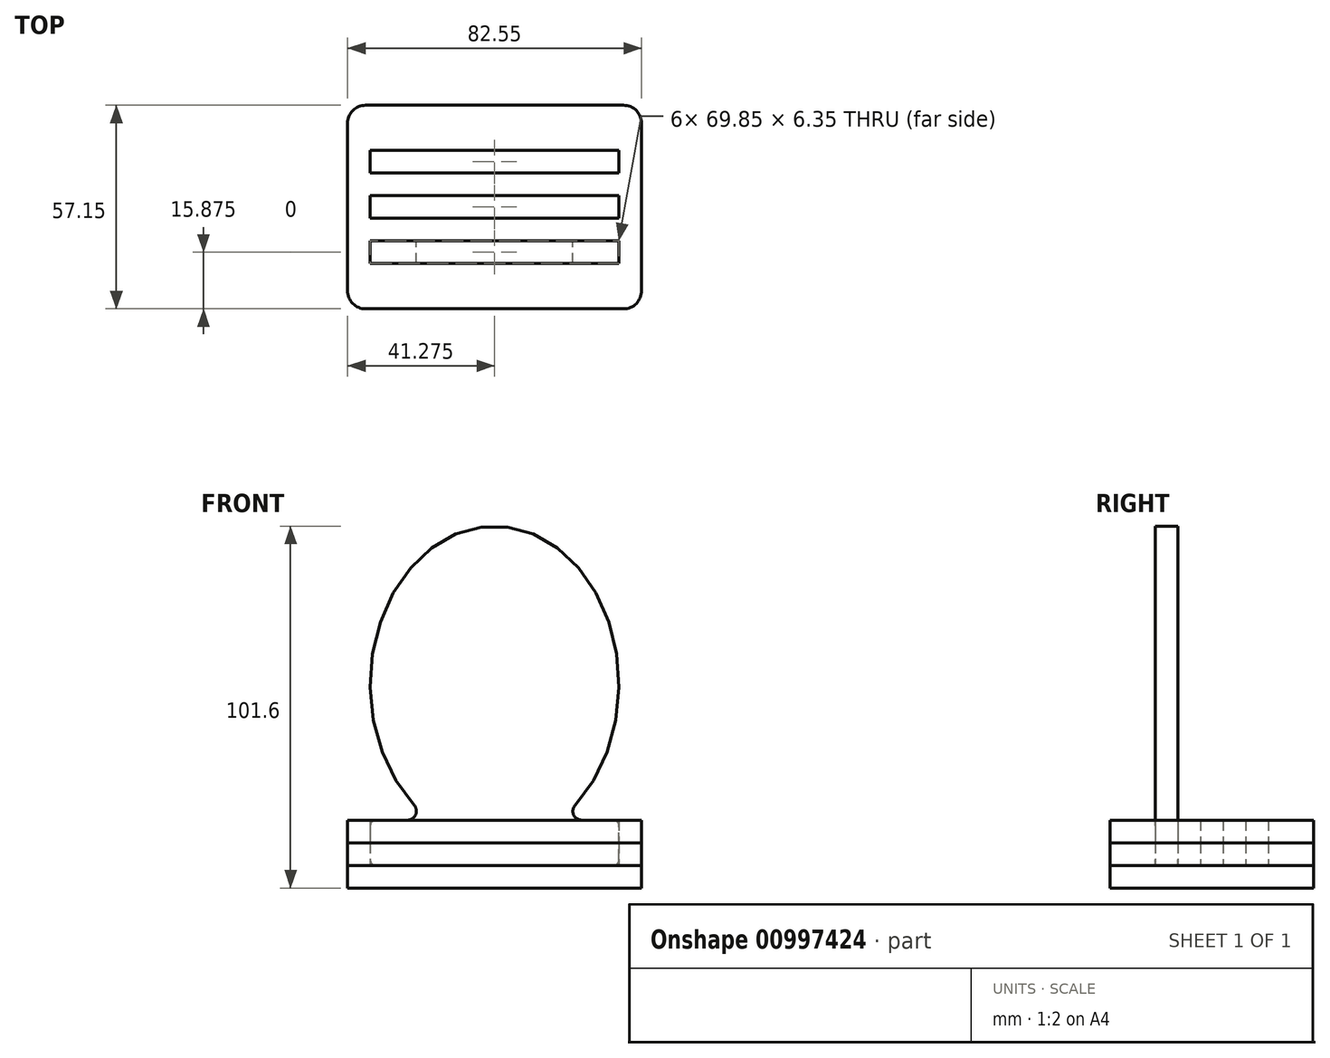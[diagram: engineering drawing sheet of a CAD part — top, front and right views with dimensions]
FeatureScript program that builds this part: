
annotation { "Feature Type Name" : "Feature", "Feature Type Description" : "" }
export const myFeature = defineFeature(function(context is Context, id is Id, definition is map)
    precondition{}
    {
        {
            var Q0;
            Q0=qCreatedBy(makeId("Top.planeOp"),FACE);
            var sketch = newSketch(context, id + "F0", { "sketchPlane" : qUnion([Q0])});
            skLineSegment(sketch, "E0.bottom", {"start": v(0, 0) * mm, "end": v(82.55, 0) * mm});
            skLineSegment(sketch, "E0.top", {"start": v(0, 57.15) * mm, "end": v(82.55, 57.15) * mm});
            skLineSegment(sketch, "E0.left", {"start": v(0, 0) * mm, "end": v(0, 57.15) * mm});
            skLineSegment(sketch, "E0.right", {"start": v(82.55, 0) * mm, "end": v(82.55, 57.15) * mm});
            skLineSegment(sketch, "E1.bottom", {"start": v(6.35, 19.05) * mm, "end": v(76.2, 19.05) * mm});
            skLineSegment(sketch, "E1.top", {"start": v(6.35, 12.7) * mm, "end": v(76.2, 12.7) * mm});
            skLineSegment(sketch, "E1.left", {"start": v(6.35, 19.05) * mm, "end": v(6.35, 12.7) * mm});
            skLineSegment(sketch, "E1.right", {"start": v(76.2, 19.05) * mm, "end": v(76.2, 12.7) * mm});
            skLineSegment(sketch, "E2.0.1.0", {"start": v(6.35, 25.4) * mm, "end": v(76.2, 25.4) * mm});
            skLineSegment(sketch, "E2.0.1.1", {"start": v(6.35, 31.75) * mm, "end": v(6.35, 25.4) * mm});
            skLineSegment(sketch, "E2.0.1.2", {"start": v(76.2, 31.75) * mm, "end": v(76.2, 25.4) * mm});
            skLineSegment(sketch, "E2.0.1.3", {"start": v(6.35, 31.75) * mm, "end": v(76.2, 31.75) * mm});
            skLineSegment(sketch, "E2.0.2.0", {"start": v(6.35, 38.1) * mm, "end": v(76.2, 38.1) * mm});
            skLineSegment(sketch, "E2.0.2.1", {"start": v(6.35, 44.45) * mm, "end": v(6.35, 38.1) * mm});
            skLineSegment(sketch, "E2.0.2.2", {"start": v(76.2, 44.45) * mm, "end": v(76.2, 38.1) * mm});
            skLineSegment(sketch, "E2.0.2.3", {"start": v(6.35, 44.45) * mm, "end": v(76.2, 44.45) * mm});
            skLineSegment(sketch, "E2.direction1", {"start": v(6.35, 12.7) * mm, "end": v(6.35, 12.7) * mm});
            skLineSegment(sketch, "E2.direction2", {"start": v(6.35, 12.7) * mm, "end": v(6.35, 25.4) * mm, "construction": true});
            skSolve(sketch);
        }
        {
            var Q0;
            Q0=makeQuery(id+"F0.imprint","IMPRINT",FACE,{"disambiguationData":[TD([[makeQuery(id+"F0.imprint","IMPRINT",EDGE,{"derivedFrom":sQuery(id+"F0.wireOp",EDGE,"E0.bottom")}),1.0]])]});
            var Q1;
            Q1=makeQuery(id+"F0.imprint","IMPRINT",FACE,{"disambiguationData":[TD([[makeQuery(id+"F0.imprint","IMPRINT",EDGE,{"derivedFrom":sQuery(id+"F0.wireOp",EDGE,"E1.bottom")}),-1.0]])]});
            var Q2;
            Q2=makeQuery(id+"F0.imprint","IMPRINT",FACE,{"disambiguationData":[TD([[makeQuery(id+"F0.imprint","IMPRINT",EDGE,{"derivedFrom":sQuery(id+"F0.wireOp",EDGE,"E2.0.1.0")}),1.0]])]});
            var Q3;
            Q3=makeQuery(id+"F0.imprint","IMPRINT",FACE,{"disambiguationData":[TD([[makeQuery(id+"F0.imprint","IMPRINT",EDGE,{"derivedFrom":sQuery(id+"F0.wireOp",EDGE,"E2.0.2.0")}),1.0]])]});
            extrude(context, id + "F1", {"entities" : qUnion([Q0, Q1, Q2, Q3]), "oppositeDirection" : true, "depth" : 6.35 * mm, "offsetDistance" : 25.4 * mm});
        }
        {
            var Q0;
            Q0=makeQuery(id+"F0.imprint","IMPRINT",FACE,{"disambiguationData":[TD([[makeQuery(id+"F0.imprint","IMPRINT",EDGE,{"derivedFrom":sQuery(id+"F0.wireOp",EDGE,"E0.bottom")}),1.0]])]});
            extrude(context, id + "F2", {"entities" : qUnion([Q0]), "depth" : 6.35 * mm, "offsetDistance" : 25.4 * mm});
        }
        {
            var Q0;
            Q0=makeQuery(id+"F2.opExtrude","CAP_FACE",FACE,{"disambiguationData":[OSD([sQuery(id+"F0.wireOp",EDGE,"E0.bottom"),sQuery(id+"F0.wireOp",EDGE,"E0.top"),sQuery(id+"F0.wireOp",EDGE,"E0.left"),sQuery(id+"F0.wireOp",EDGE,"E0.right"),sQuery(id+"F0.wireOp",EDGE,"E1.bottom"),sQuery(id+"F0.wireOp",EDGE,"E1.top"),sQuery(id+"F0.wireOp",EDGE,"E1.left"),sQuery(id+"F0.wireOp",EDGE,"E1.right"),sQuery(id+"F0.wireOp",EDGE,"E2.0.1.0"),sQuery(id+"F0.wireOp",EDGE,"E2.0.1.1"),sQuery(id+"F0.wireOp",EDGE,"E2.0.1.2"),sQuery(id+"F0.wireOp",EDGE,"E2.0.1.3"),sQuery(id+"F0.wireOp",EDGE,"E2.0.2.0"),sQuery(id+"F0.wireOp",EDGE,"E2.0.2.1"),sQuery(id+"F0.wireOp",EDGE,"E2.0.2.2"),sQuery(id+"F0.wireOp",EDGE,"E2.0.2.3")])],"isStart":false});
            extrude(context, id + "F3", {"entities" : qUnion([Q0]), "depth" : 6.35 * mm, "offsetDistance" : 25.4 * mm});
        }
        {
            var Q0;
            Q0=makeQuery(id+"F3.opExtrude","SWEPT_EDGE",EDGE,{"disambiguationData":[OSD([sQuery(id+"F0.wireOp",EDGE,"E0.bottom"),sQuery(id+"F0.wireOp",EDGE,"E0.right")])]});
            var Q1;
            Q1=makeQuery(id+"F2.opExtrude","SWEPT_EDGE",EDGE,{"disambiguationData":[OSD([sQuery(id+"F0.wireOp",EDGE,"E0.bottom"),sQuery(id+"F0.wireOp",EDGE,"E0.right")])]});
            var Q2;
            Q2=makeQuery(id+"F1.opExtrude","SWEPT_EDGE",EDGE,{"disambiguationData":[OSD([sQuery(id+"F0.wireOp",EDGE,"E0.bottom"),sQuery(id+"F0.wireOp",EDGE,"E0.right")])]});
            var Q3;
            Q3=makeQuery(id+"F3.opExtrude","SWEPT_EDGE",EDGE,{"disambiguationData":[OSD([sQuery(id+"F0.wireOp",EDGE,"E0.bottom"),sQuery(id+"F0.wireOp",EDGE,"E0.left")])]});
            var Q4;
            Q4=makeQuery(id+"F2.opExtrude","SWEPT_EDGE",EDGE,{"disambiguationData":[OSD([sQuery(id+"F0.wireOp",EDGE,"E0.bottom"),sQuery(id+"F0.wireOp",EDGE,"E0.left")])]});
            var Q5;
            Q5=makeQuery(id+"F1.opExtrude","SWEPT_EDGE",EDGE,{"disambiguationData":[OSD([sQuery(id+"F0.wireOp",EDGE,"E0.bottom"),sQuery(id+"F0.wireOp",EDGE,"E0.left")])]});
            var Q6;
            Q6=makeQuery(id+"F3.opExtrude","SWEPT_EDGE",EDGE,{"disambiguationData":[OSD([sQuery(id+"F0.wireOp",EDGE,"E0.top"),sQuery(id+"F0.wireOp",EDGE,"E0.left")])]});
            var Q7;
            Q7=makeQuery(id+"F2.opExtrude","SWEPT_EDGE",EDGE,{"disambiguationData":[OSD([sQuery(id+"F0.wireOp",EDGE,"E0.top"),sQuery(id+"F0.wireOp",EDGE,"E0.left")])]});
            var Q8;
            Q8=makeQuery(id+"F1.opExtrude","SWEPT_EDGE",EDGE,{"disambiguationData":[OSD([sQuery(id+"F0.wireOp",EDGE,"E0.top"),sQuery(id+"F0.wireOp",EDGE,"E0.left")])]});
            var Q9;
            Q9=makeQuery(id+"F3.opExtrude","SWEPT_EDGE",EDGE,{"disambiguationData":[OSD([sQuery(id+"F0.wireOp",EDGE,"E0.top"),sQuery(id+"F0.wireOp",EDGE,"E0.right")])]});
            var Q10;
            Q10=makeQuery(id+"F2.opExtrude","SWEPT_EDGE",EDGE,{"disambiguationData":[OSD([sQuery(id+"F0.wireOp",EDGE,"E0.top"),sQuery(id+"F0.wireOp",EDGE,"E0.right")])]});
            var Q11;
            Q11=makeQuery(id+"F1.opExtrude","SWEPT_EDGE",EDGE,{"disambiguationData":[OSD([sQuery(id+"F0.wireOp",EDGE,"E0.top"),sQuery(id+"F0.wireOp",EDGE,"E0.right")])]});
            fillet(context, id + "F4", {"entities" : qUnion([Q0, Q1, Q2, Q3, Q4, Q5, Q6, Q7, Q8, Q9, Q10, Q11]), "radius" : 5.08 * mm, "tangentPropagation" : true, "allowEdgeOverflow" : false});
        }
        {
            var Q0;
            Q0=makeQuery(id+"F3.opExtrude","SWEPT_FACE",FACE,{"disambiguationData":[OSD([sQuery(id+"F0.wireOp",EDGE,"E1.bottom")])]});
            var sketch = newSketch(context, id + "F5", { "sketchPlane" : qUnion([Q0])});
            skLineSegment(sketch, "E3.0.0", {"start": v(6.35, 0) * mm, "end": v(76.2, 0) * mm});
            skLineSegment(sketch, "E3.0.1", {"start": v(76.2, 0) * mm, "end": v(76.2, 6.35) * mm});
            skLineSegment(sketch, "E3.0.2", {"start": v(76.2, 6.35) * mm, "end": v(6.35, 6.35) * mm});
            skLineSegment(sketch, "E3.0.3", {"start": v(6.35, 6.35) * mm, "end": v(6.35, 0) * mm});
            skLineSegment(sketch, "E4.bottom", {"start": v(6.35, 12.7) * mm, "end": v(76.2, 12.7) * mm});
            skLineSegment(sketch, "E4.top", {"start": v(6.35, 6.35) * mm, "end": v(76.2, 6.35) * mm});
            skLineSegment(sketch, "E4.left", {"start": v(6.35, 12.7) * mm, "end": v(6.35, 6.35) * mm});
            skLineSegment(sketch, "E4.right", {"start": v(76.2, 12.7) * mm, "end": v(76.2, 6.35) * mm});
            skEllipse(sketch, "E5", {"center": v(41.28, 50.8) * mm, "majorRadius": 44.45 * mm, "minorRadius": 34.93 * mm, "majorAxis": v(0, 1)});
            skLineSegment(sketch, "E6", {"start": v(41.28, 0) * mm, "end": v(41.28, 109.72) * mm, "construction": true});
            skPoint(sketch, "E7", {"position": v(41.28, 54.86) * mm});
            skFitSpline(sketch, "E8.0", {"points": [v(42.6, 88.87) * mm, v(41.27, 88.91) * mm, v(39.94, 88.87) * mm, v(38.18, 88.7) * mm, v(35.99, 88.29) * mm, v(33.4, 87.46) * mm, v(30.86, 86.3) * mm, v(28.38, 84.82) * mm, v(25.99, 83) * mm, v(24.08, 81.2) * mm, v(22.62, 79.6) * mm, v(21.56, 78.32) * mm, v(20.55, 76.96) * mm, v(19.27, 75.07) * mm, v(17.8, 72.55) * mm, v(16.28, 69.3) * mm, v(15, 65.87) * mm, v(14, 62.27) * mm, v(13.25, 58.54) * mm, v(12.88, 55.35) * mm, v(12.73, 52.76) * mm, v(12.69, 50.8) * mm, v(12.73, 48.84) * mm, v(12.88, 46.25) * mm, v(13.25, 43.06) * mm, v(14, 39.33) * mm, v(15, 35.73) * mm, v(16.28, 32.3) * mm, v(17.8, 29.05) * mm, v(19.27, 26.53) * mm, v(20.55, 24.64) * mm, v(21.56, 23.28) * mm, v(22.62, 22) * mm, v(24.08, 20.4) * mm, v(25.99, 18.6) * mm, v(28.38, 16.78) * mm, v(30.86, 15.3) * mm, v(33.4, 14.14) * mm, v(35.99, 13.31) * mm, v(38.18, 12.9) * mm, v(39.94, 12.73) * mm, v(41.28, 12.69) * mm, v(42.6, 12.73) * mm, v(44.37, 12.9) * mm, v(46.56, 13.31) * mm, v(49.15, 14.14) * mm, v(51.69, 15.3) * mm, v(54.17, 16.78) * mm, v(56.56, 18.6) * mm, v(58.47, 20.4) * mm, v(59.93, 22) * mm, v(60.99, 23.28) * mm, v(62, 24.64) * mm, v(63.28, 26.53) * mm, v(64.75, 29.05) * mm, v(66.27, 32.3) * mm, v(67.55, 35.73) * mm, v(68.56, 39.33) * mm, v(69.3, 43.06) * mm, v(69.67, 46.25) * mm, v(69.82, 48.84) * mm, v(69.86, 50.8) * mm, v(69.82, 52.76) * mm, v(69.67, 55.35) * mm, v(69.3, 58.54) * mm, v(68.56, 62.27) * mm, v(67.55, 65.87) * mm, v(66.27, 69.3) * mm, v(64.75, 72.55) * mm, v(63.28, 75.07) * mm, v(62, 76.96) * mm, v(60.99, 78.32) * mm, v(59.93, 79.6) * mm, v(58.47, 81.2) * mm, v(56.56, 83) * mm, v(54.17, 84.82) * mm, v(51.69, 86.3) * mm, v(49.15, 87.46) * mm, v(46.56, 88.29) * mm, v(44.37, 88.7) * mm, v(42.6, 88.87) * mm, v(41.27, 88.91) * mm, v(39.94, 88.87) * mm, v(42.6, 88.87) * mm]});
            skSolve(sketch);
        }
        {
            var Q0;
            Q0 = qSketchRegion(id + "F5", true);
            extrude(context, id + "F6", {"entities" : qUnion([Q0]), "depth" : 6.35 * mm, "offsetDistance" : 25.4 * mm});
        }
        {
            var Q0;
            {var subQ0=sQuery(id+"F5.wireOp",EDGE,"E5");var subQ1=sQuery(id+"F5.wireOp",EDGE,"E4.bottom");Q0=makeQuery(id+"F6.opExtrude","SWEPT_EDGE",EDGE,{"disambiguationData":[OSD([subQ1,subQ0]),TDD([makeQuery(id+"F5.imprint","INTERSECT",VERTEX,{"disambiguationData":[OD(1.0)],"derivedFrom":[subQ1,subQ0]})])]});}
            var Q1;
            {var subQ0=sQuery(id+"F5.wireOp",EDGE,"E5");var subQ1=sQuery(id+"F5.wireOp",EDGE,"E4.bottom");Q1=makeQuery(id+"F6.opExtrude","SWEPT_EDGE",EDGE,{"disambiguationData":[OSD([subQ1,subQ0]),TDD([makeQuery(id+"F5.imprint","INTERSECT",VERTEX,{"disambiguationData":[OD(0.0)],"derivedFrom":[subQ1,subQ0]})])]});}
            fillet(context, id + "F7", {"entities" : qUnion([Q0, Q1]), "radius" : 2.54 * mm, "tangentPropagation" : true, "allowEdgeOverflow" : false});
        }
        {
            var Q0;
            Q0=makeQuery(id+"F6.opExtrude","SWEPT_EDGE",EDGE,{"disambiguationData":[OSD([sQuery(id+"F5.wireOp",EDGE,"E4.bottom"),sQuery(id+"F5.wireOp",EDGE,"E4.right")])]});
            var Q1;
            Q1=makeQuery(id+"F6.opExtrude","SWEPT_EDGE",EDGE,{"disambiguationData":[OSD([sQuery(id+"F5.wireOp",EDGE,"E4.bottom"),sQuery(id+"F5.wireOp",EDGE,"E4.left")])]});
            var Q2;
            Q2=makeQuery(id+"F6.opExtrude","SWEPT_EDGE",EDGE,{"disambiguationData":[OSD([sQuery(id+"F5.wireOp",EDGE,"E3.0.0"),sQuery(id+"F5.wireOp",EDGE,"E3.0.1")])]});
            var Q3;
            Q3=makeQuery(id+"F6.opExtrude","SWEPT_EDGE",EDGE,{"disambiguationData":[OSD([sQuery(id+"F5.wireOp",EDGE,"E3.0.0"),sQuery(id+"F5.wireOp",EDGE,"E3.0.3")])]});
            fillet(context, id + "F8", {"entities" : qUnion([Q0, Q1, Q2, Q3]), "radius" : 1.59 * mm, "tangentPropagation" : true, "allowEdgeOverflow" : false});
        }
    });
